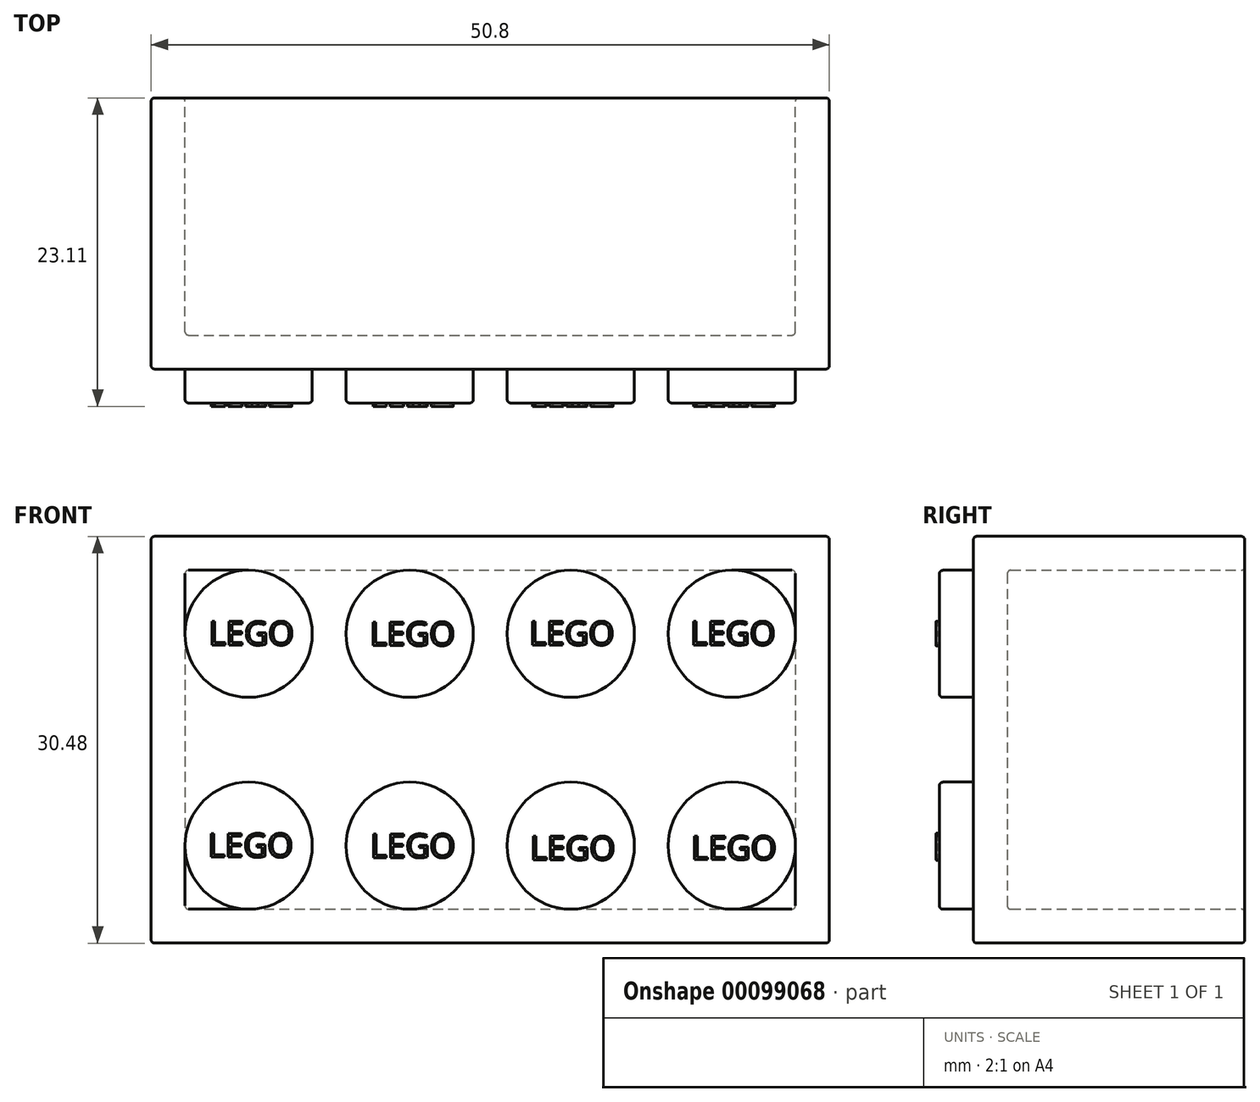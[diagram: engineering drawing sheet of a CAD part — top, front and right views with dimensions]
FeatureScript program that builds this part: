
annotation { "Feature Type Name" : "Feature", "Feature Type Description" : "" }
export const myFeature = defineFeature(function(context is Context, id is Id, definition is map)
    precondition{}
    {
        {
            var Q0;
            Q0=qCreatedBy(makeId("Front.planeOp"),FACE);
            var sketch = newSketch(context, id + "F0", { "sketchPlane" : qUnion([Q0])});
            skLineSegment(sketch, "E0.bottom", {"start": v(-21.08, 12.4) * mm, "end": v(29.72, 12.4) * mm});
            skLineSegment(sketch, "E0.top", {"start": v(-21.08, -18.08) * mm, "end": v(29.72, -18.08) * mm});
            skLineSegment(sketch, "E0.left", {"start": v(-21.08, 12.4) * mm, "end": v(-21.08, -18.08) * mm});
            skLineSegment(sketch, "E0.right", {"start": v(29.72, 12.4) * mm, "end": v(29.72, -18.08) * mm});
            skSolve(sketch);
        }
        {
            var Q0;
            Q0=makeQuery(id+"F0.imprint","IMPRINT",FACE,{"disambiguationData":[TD([[makeQuery(id+"F0.imprint","IMPRINT",EDGE,{"derivedFrom":sQuery(id+"F0.wireOp",EDGE,"E0.bottom")}),-1.0]])]});
            extrude(context, id + "F1", {"entities" : qUnion([Q0]), "depth" : 20.32 * mm});
        }
        {
            var Q0;
            Q0=makeQuery(id+"F1.opExtrude","CAP_FACE",FACE,{"disambiguationData":[OSD([sQuery(id+"F0.wireOp",EDGE,"E0.bottom"),sQuery(id+"F0.wireOp",EDGE,"E0.top"),sQuery(id+"F0.wireOp",EDGE,"E0.left"),sQuery(id+"F0.wireOp",EDGE,"E0.right")])],"isStart":true});
            shell(context, id + "F2", {"entities" : qUnion([Q0]), "thickness" : 2.54 * mm});
        }
        {
            var Q0;
            Q0=makeQuery(id+"F1.opExtrude","CAP_FACE",FACE,{"disambiguationData":[OSD([sQuery(id+"F0.wireOp",EDGE,"E0.bottom"),sQuery(id+"F0.wireOp",EDGE,"E0.top"),sQuery(id+"F0.wireOp",EDGE,"E0.left"),sQuery(id+"F0.wireOp",EDGE,"E0.right")])],"isStart":false});
            var sketch = newSketch(context, id + "F3", { "sketchPlane" : qUnion([Q0])});
            skCircle(sketch, "E1", {"center": v(22.42, -10.77) * mm, "radius": 4.76 * mm});
            skCircle(sketch, "E2", {"center": v(22.42, 5.1) * mm, "radius": 4.76 * mm});
            skCircle(sketch, "E3", {"center": v(10.35, 5.1) * mm, "radius": 4.76 * mm});
            skCircle(sketch, "E4", {"center": v(10.35, -10.77) * mm, "radius": 4.76 * mm});
            skLineSegment(sketch, "E5", {"start": v(4.32, 12.4) * mm, "end": v(4.32, -18.08) * mm});
            skCircle(sketch, "E6.MirrorC", {"center": v(-13.78, 5.1) * mm, "radius": 4.76 * mm});
            skCircle(sketch, "E7.MirrorC", {"center": v(-1.71, 5.1) * mm, "radius": 4.76 * mm});
            skCircle(sketch, "E8.MirrorC", {"center": v(-1.71, -10.77) * mm, "radius": 4.76 * mm});
            skCircle(sketch, "E9.MirrorC", {"center": v(-13.78, -10.77) * mm, "radius": 4.76 * mm});
            skSolve(sketch);
        }
        {
            var Q0;
            Q0 = qSketchRegion(id + "F3", true);
            extrude(context, id + "F4", {"entities" : qUnion([Q0]), "operationType" : NewBodyOperationType.ADD, "depth" : 2.54 * mm});
        }
        {
            var Q0;
            Q0=makeQuery(id+"F4.opExtrude","CAP_EDGE",EDGE,{"disambiguationData":[OSD([sQuery(id+"F3.wireOp",EDGE,"E8.MirrorC")])],"isStart":false});
            var Q1;
            Q1=makeQuery(id+"F4.opExtrude","CAP_EDGE",EDGE,{"disambiguationData":[OSD([sQuery(id+"F3.wireOp",EDGE,"E4")])],"isStart":false});
            var Q2;
            Q2=makeQuery(id+"F4.opExtrude","CAP_EDGE",EDGE,{"disambiguationData":[OSD([sQuery(id+"F3.wireOp",EDGE,"E1")])],"isStart":false});
            var Q3;
            Q3=makeQuery(id+"F4.opExtrude","CAP_EDGE",EDGE,{"disambiguationData":[OSD([sQuery(id+"F3.wireOp",EDGE,"E2")])],"isStart":false});
            var Q4;
            Q4=makeQuery(id+"F4.opExtrude","CAP_EDGE",EDGE,{"disambiguationData":[OSD([sQuery(id+"F3.wireOp",EDGE,"E3")])],"isStart":false});
            var Q5;
            Q5=makeQuery(id+"F4.opExtrude","CAP_EDGE",EDGE,{"disambiguationData":[OSD([sQuery(id+"F3.wireOp",EDGE,"E1")])],"isStart":true});
            var Q6;
            Q6=makeQuery(id+"F4.opExtrude","CAP_EDGE",EDGE,{"disambiguationData":[OSD([sQuery(id+"F3.wireOp",EDGE,"E2")])],"isStart":true});
            var Q7;
            Q7=makeQuery(id+"F4.opExtrude","CAP_EDGE",EDGE,{"disambiguationData":[OSD([sQuery(id+"F3.wireOp",EDGE,"E4")])],"isStart":true});
            var Q8;
            Q8=makeQuery(id+"F4.opExtrude","CAP_EDGE",EDGE,{"disambiguationData":[OSD([sQuery(id+"F3.wireOp",EDGE,"E3")])],"isStart":true});
            var Q9;
            Q9=makeQuery(id+"F4.opExtrude","CAP_EDGE",EDGE,{"disambiguationData":[OSD([sQuery(id+"F3.wireOp",EDGE,"E8.MirrorC")])],"isStart":true});
            var Q10;
            Q10=makeQuery(id+"F4.opExtrude","CAP_EDGE",EDGE,{"disambiguationData":[OSD([sQuery(id+"F3.wireOp",EDGE,"E9.MirrorC")])],"isStart":true});
            var Q11;
            Q11=makeQuery(id+"F4.opExtrude","CAP_EDGE",EDGE,{"disambiguationData":[OSD([sQuery(id+"F3.wireOp",EDGE,"E6.MirrorC")])],"isStart":true});
            var Q12;
            Q12=makeQuery(id+"F4.opExtrude","CAP_EDGE",EDGE,{"disambiguationData":[OSD([sQuery(id+"F3.wireOp",EDGE,"E7.MirrorC")])],"isStart":true});
            var Q13;
            Q13=makeQuery(id+"F4.opExtrude","CAP_EDGE",EDGE,{"disambiguationData":[OSD([sQuery(id+"F3.wireOp",EDGE,"E7.MirrorC")])],"isStart":false});
            var Q14;
            Q14=makeQuery(id+"F4.opExtrude","CAP_EDGE",EDGE,{"disambiguationData":[OSD([sQuery(id+"F3.wireOp",EDGE,"E6.MirrorC")])],"isStart":false});
            var Q15;
            Q15=makeQuery(id+"F4.opExtrude","CAP_EDGE",EDGE,{"disambiguationData":[OSD([sQuery(id+"F3.wireOp",EDGE,"E9.MirrorC")])],"isStart":false});
            var Q16;
            Q16=makeQuery(id+"F1.opExtrude","CAP_EDGE",EDGE,{"disambiguationData":[OSD([sQuery(id+"F0.wireOp",EDGE,"E0.top")])],"isStart":false});
            var Q17;
            Q17=makeQuery(id+"F1.opExtrude","SWEPT_FACE",FACE,{"disambiguationData":[OSD([sQuery(id+"F0.wireOp",EDGE,"E0.left")])]});
            var Q18;
            Q18=makeQuery(id+"F1.opExtrude","SWEPT_FACE",FACE,{"disambiguationData":[OSD([sQuery(id+"F0.wireOp",EDGE,"E0.right")])]});
            var Q19;
            Q19=makeQuery(id+"F1.opExtrude","SWEPT_FACE",FACE,{"disambiguationData":[OSD([sQuery(id+"F0.wireOp",EDGE,"E0.bottom")])]});
            var Q20;
            Q20=makeQuery(id+"F1.opExtrude","CAP_FACE",FACE,{"disambiguationData":[OSD([sQuery(id+"F0.wireOp",EDGE,"E0.bottom"),sQuery(id+"F0.wireOp",EDGE,"E0.top"),sQuery(id+"F0.wireOp",EDGE,"E0.left"),sQuery(id+"F0.wireOp",EDGE,"E0.right")])],"isStart":true});
            var Q21;
            Q21=makeQuery(id+"F2.opShell","OFFSET_EDGE",EDGE,{"disambiguationData":[OSD([sQuery(id+"F0.wireOp",EDGE,"E0.bottom"),sQuery(id+"F0.wireOp",EDGE,"E0.right")])]});
            var Q22;
            {var subQ0=sQuery(id+"F0.wireOp",EDGE,"E0.right");Q22=makeQuery(id+"F2.opShell","OFFSET_EDGE",EDGE,{"disambiguationData":[OSD([subQ0]),TDD([makeQuery(id+"F1.opExtrude","CAP_EDGE",EDGE,{"disambiguationData":[OSD([subQ0])],"isStart":false})])]});}
            var Q23;
            Q23=makeQuery(id+"F2.opShell","OFFSET_FACE",FACE,{"disambiguationData":[OSD([sQuery(id+"F0.wireOp",EDGE,"E0.bottom"),sQuery(id+"F0.wireOp",EDGE,"E0.top"),sQuery(id+"F0.wireOp",EDGE,"E0.left"),sQuery(id+"F0.wireOp",EDGE,"E0.right")])]});
            var Q24;
            Q24=makeQuery(id+"F2.opShell","OFFSET_FACE",FACE,{"disambiguationData":[OSD([sQuery(id+"F0.wireOp",EDGE,"E0.left")])]});
            var Q25;
            {var subQ0=sQuery(id+"F0.wireOp",EDGE,"E0.bottom");Q25=makeQuery(id+"F2.opShell","OFFSET_EDGE",EDGE,{"disambiguationData":[OSD([subQ0]),TDD([makeQuery(id+"F1.opExtrude","CAP_EDGE",EDGE,{"disambiguationData":[OSD([subQ0])],"isStart":true})])]});}
            var Q26;
            Q26=makeQuery(id+"F2.opShell","OFFSET_FACE",FACE,{"disambiguationData":[OSD([sQuery(id+"F0.wireOp",EDGE,"E0.top")])]});
            fillet(context, id + "F5", {"entities" : qUnion([Q0, Q1, Q2, Q3, Q4, Q5, Q6, Q7, Q8, Q9, Q10, Q11, Q12, Q13, Q14, Q15, Q16, Q17, Q18, Q19, Q20, Q21, Q22, Q23, Q24, Q25, Q26]), "radius" : 0.25 * mm, "tangentPropagation" : true, "allowEdgeOverflow" : false});
        }
        {
            var Q0;
            Q0=makeQuery(id+"F4.opExtrude","CAP_FACE",FACE,{"disambiguationData":[OSD([sQuery(id+"F3.wireOp",EDGE,"E6.MirrorC")])],"isStart":false});
            var sketch = newSketch(context, id + "F6", { "sketchPlane" : qUnion([Q0])});
            skText(sketch, "E10", { "text": "LEGO\n", "fontName": "OpenSans-Regular.ttf"});
            skText(sketch, "E11", { "text": "LEGO\n", "fontName": "OpenSans-Regular.ttf"});
            skText(sketch, "E12", { "text": "LEGO\n", "fontName": "OpenSans-Regular.ttf"});
            skText(sketch, "E13", { "text": "LEGO\n", "fontName": "OpenSans-Regular.ttf"});
            skText(sketch, "E14", { "text": "LEGO\n", "fontName": "OpenSans-Regular.ttf"});
            skText(sketch, "E15", { "text": "LEGO\n", "fontName": "OpenSans-Regular.ttf"});
            skText(sketch, "E16", { "text": "LEGO\n", "fontName": "OpenSans-Regular.ttf"});
            skText(sketch, "E17", { "text": "LEGO\n", "fontName": "OpenSans-Regular.ttf"});
            const initialGuessF6  = {"E10": [-0.01677, 0.00426, 1, 0, 0.00178], "E11": [-0.0047, 0.00422, 1, 0, 0.00178], "E12": [0.00723, 0.00426, 1, 0, 0.00178], "E13": [0.0193, 0.00426, 1, 0, 0.00178], "E14": [-0.01683, -0.01163, 1, 0, 0.00178], "E15": [-0.00468, -0.01167, 1, 0, 0.00178], "E16": [0.0073, -0.01184, 1, 0, 0.00178], "E17": [0.01938, -0.01182, 1, 0, 0.00178]};
            skSetInitialGuess(sketch, initialGuessF6);
            skSolve(sketch);
        }
        {
            var Q0;
            Q0 = qSketchRegion(id + "F6", true);
            extrude(context, id + "F7", {"entities" : qUnion([Q0]), "operationType" : NewBodyOperationType.ADD, "depth" : 0.25 * mm});
        }
    });
